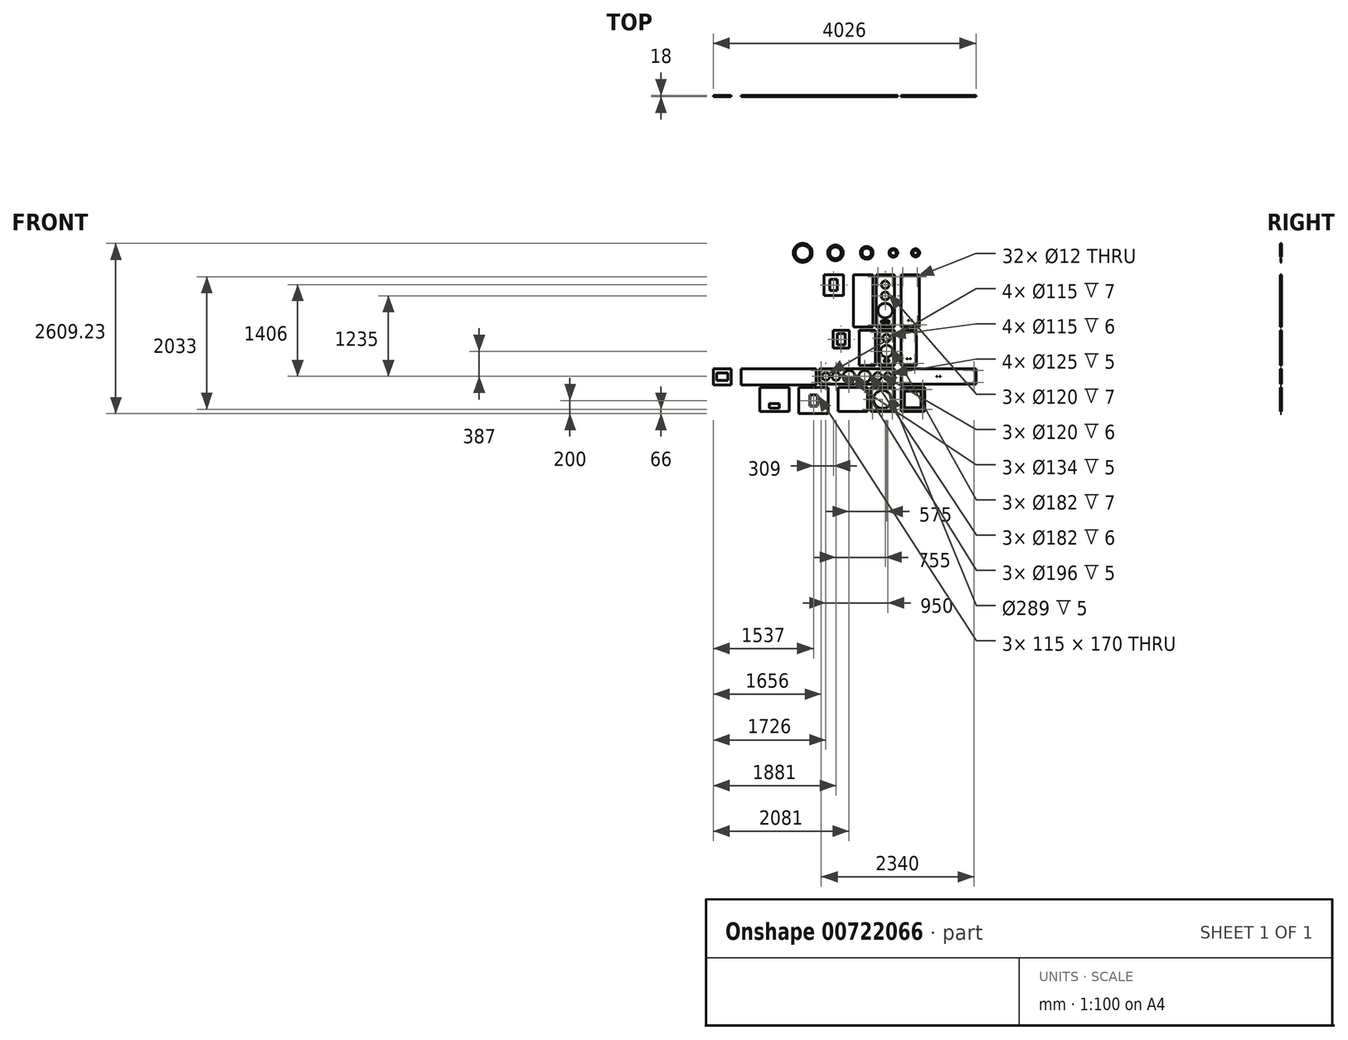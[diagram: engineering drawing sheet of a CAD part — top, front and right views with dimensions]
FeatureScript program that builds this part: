
annotation { "Feature Type Name" : "Feature", "Feature Type Description" : "" }
export const myFeature = defineFeature(function(context is Context, id is Id, definition is map)
    precondition{}
    {
        {
            assignVariable(context, id + "F0", {"name" : "WoodW", "anyValue" : 18});
        }
        {
            var Q0;
            Q0=qCreatedBy(makeId("Front.planeOp"),FACE);
            var sketch = newSketch(context, id + "F1", { "sketchPlane" : qUnion([Q0])});
            skLineSegment(sketch, "E0.bottom", {"start": v(0, 400) * mm, "end": v(-280, 400) * mm});
            skLineSegment(sketch, "E0.top", {"start": v(0, -400) * mm, "end": v(-280, -400) * mm});
            skLineSegment(sketch, "E0.left", {"start": v(0, 400) * mm, "end": v(0, -400) * mm});
            skLineSegment(sketch, "E0.right", {"start": v(-280, 400) * mm, "end": v(-280, -400) * mm});
            skLineSegment(sketch, "E1", {"start": v(-140, 400) * mm, "end": v(-140, -400) * mm, "construction": true});
            skCircle(sketch, "E2", {"center": v(-250, 370) * mm, "radius": 6 * mm});
            skCircle(sketch, "E3.MirrorC", {"center": v(-30, 370) * mm, "radius": 6 * mm});
            skCircle(sketch, "E4.MirrorC", {"center": v(-30, -370) * mm, "radius": 6 * mm});
            skCircle(sketch, "E5.MirrorC", {"center": v(-250, -370) * mm, "radius": 6 * mm});
            skLineSegment(sketch, "E6", {"start": v(50, 227.38) * mm, "end": v(50, -1997.12) * mm, "construction": true});
            skCircle(sketch, "E7.MirrorC", {"center": v(350, -370) * mm, "radius": 6 * mm});
            skCircle(sketch, "E8.MirrorC", {"center": v(130, -370) * mm, "radius": 6 * mm});
            skCircle(sketch, "E9.MirrorC", {"center": v(130, 370) * mm, "radius": 6 * mm});
            skCircle(sketch, "E10.MirrorC", {"center": v(350, 370) * mm, "radius": 6 * mm});
            skLineSegment(sketch, "E11.MirrorCS", {"start": v(100, 400) * mm, "end": v(380, 400) * mm});
            skLineSegment(sketch, "E12.MirrorCS", {"start": v(100, -400) * mm, "end": v(380, -400) * mm});
            skLineSegment(sketch, "E13.MirrorCS", {"start": v(100, 400) * mm, "end": v(100, -400) * mm});
            skLineSegment(sketch, "E14.MirrorCS", {"start": v(380, 400) * mm, "end": v(380, -400) * mm});
            skCircle(sketch, "E15", {"center": v(-140, -150) * mm, "radius": 112.5 * mm});
            skCircle(sketch, "E16", {"center": v(-140, 76) * mm, "radius": 60 * mm});
            skCircle(sketch, "E17", {"center": v(-140, 247) * mm, "radius": 57.5 * mm});
            skCircle(sketch, "E18.1.0", {"center": v(215, -300) * mm, "radius": 3.5 * mm});
            skLineSegment(sketch, "E19.bottom", {"start": v(-196, -305) * mm, "end": v(-84, -305) * mm});
            skLineSegment(sketch, "E19.top", {"start": v(-196, -345) * mm, "end": v(-84, -345) * mm});
            skLineSegment(sketch, "E19.left", {"start": v(-200, -309) * mm, "end": v(-200, -341) * mm});
            skLineSegment(sketch, "E19.right", {"start": v(-80, -309) * mm, "end": v(-80, -341) * mm});
            skPoint(sketch, "E20", {"position": v(-140, -305) * mm});
            skPoint(sketch, "E21.visualSharp", {"position": v(-200, -305) * mm});
            skArc(sketch, "E21.filletArc", {"start": v(-196, -305) * mm, "mid": v(-198.83, -306.17) * mm, "end": v(-200, -309) * mm});
            skPoint(sketch, "E22.visualSharp", {"position": v(-200, -345) * mm});
            skArc(sketch, "E22.filletArc", {"start": v(-200, -341) * mm, "mid": v(-198.83, -343.83) * mm, "end": v(-196, -345) * mm});
            skPoint(sketch, "E23.visualSharp", {"position": v(-80, -345) * mm});
            skArc(sketch, "E23.filletArc", {"start": v(-84, -345) * mm, "mid": v(-81.17, -343.83) * mm, "end": v(-80, -341) * mm});
            skPoint(sketch, "E24.visualSharp", {"position": v(-80, -305) * mm});
            skArc(sketch, "E24.filletArc", {"start": v(-80, -309) * mm, "mid": v(-81.17, -306.17) * mm, "end": v(-84, -305) * mm});
            skLineSegment(sketch, "E25.bottom", {"start": v(0, -450) * mm, "end": v(-240, -450) * mm});
            skLineSegment(sketch, "E25.top", {"start": v(0, -989) * mm, "end": v(-240, -989) * mm});
            skLineSegment(sketch, "E25.left", {"start": v(0, -450) * mm, "end": v(0, -989) * mm});
            skLineSegment(sketch, "E25.right", {"start": v(-240, -450) * mm, "end": v(-240, -989) * mm});
            skLineSegment(sketch, "E26", {"start": v(-120, -450) * mm, "end": v(-120, -989) * mm, "construction": true});
            skCircle(sketch, "E27", {"center": v(-120, -571) * mm, "radius": 57.5 * mm});
            skCircle(sketch, "E28", {"center": v(-120, -772) * mm, "radius": 91 * mm});
            skCircle(sketch, "E29", {"center": v(-210, -480) * mm, "radius": 6 * mm});
            skLineSegment(sketch, "E30", {"start": v(-240, -719.5) * mm, "end": v(0, -719.5) * mm, "construction": true});
            skCircle(sketch, "E31.MirrorC", {"center": v(-210, -959) * mm, "radius": 6 * mm});
            skCircle(sketch, "E32.MirrorC", {"center": v(-30, -959) * mm, "radius": 6 * mm});
            skCircle(sketch, "E33.MirrorC", {"center": v(-30, -480) * mm, "radius": 6 * mm});
            skLineSegment(sketch, "E34.MirrorCS", {"start": v(100, -450) * mm, "end": v(100, -989) * mm});
            skLineSegment(sketch, "E35.MirrorCS", {"start": v(100, -450) * mm, "end": v(340, -450) * mm});
            skLineSegment(sketch, "E36.MirrorCS", {"start": v(340, -450) * mm, "end": v(340, -989) * mm});
            skLineSegment(sketch, "E37.MirrorCS", {"start": v(100, -989) * mm, "end": v(340, -989) * mm});
            skCircle(sketch, "E38.MirrorC", {"center": v(130, -959) * mm, "radius": 6 * mm});
            skCircle(sketch, "E39.MirrorC", {"center": v(310, -959) * mm, "radius": 6 * mm});
            skCircle(sketch, "E40.MirrorC", {"center": v(130, -480) * mm, "radius": 6 * mm});
            skCircle(sketch, "E41.MirrorC", {"center": v(310, -480) * mm, "radius": 6 * mm});
            skLineSegment(sketch, "E42.bottom", {"start": v(-153.5, -904) * mm, "end": v(-86.5, -904) * mm});
            skLineSegment(sketch, "E42.top", {"start": v(-153.5, -934) * mm, "end": v(-86.5, -934) * mm});
            skLineSegment(sketch, "E42.left", {"start": v(-157.5, -908) * mm, "end": v(-157.5, -930) * mm});
            skLineSegment(sketch, "E42.right", {"start": v(-82.5, -908) * mm, "end": v(-82.5, -930) * mm});
            skPoint(sketch, "E43", {"position": v(-120, -904) * mm});
            skLineSegment(sketch, "E44", {"start": v(220, -450) * mm, "end": v(220, -989) * mm, "construction": true});
            skPoint(sketch, "E45.visualSharp", {"position": v(-157.5, -904) * mm});
            skArc(sketch, "E45.filletArc", {"start": v(-153.5, -904) * mm, "mid": v(-156.33, -905.17) * mm, "end": v(-157.5, -908) * mm});
            skPoint(sketch, "E46.visualSharp", {"position": v(-157.5, -934) * mm});
            skArc(sketch, "E46.filletArc", {"start": v(-157.5, -930) * mm, "mid": v(-156.33, -932.83) * mm, "end": v(-153.5, -934) * mm});
            skPoint(sketch, "E47.visualSharp", {"position": v(-82.5, -934) * mm});
            skArc(sketch, "E47.filletArc", {"start": v(-86.5, -934) * mm, "mid": v(-83.67, -932.83) * mm, "end": v(-82.5, -930) * mm});
            skPoint(sketch, "E48.visualSharp", {"position": v(-82.5, -904) * mm});
            skArc(sketch, "E48.filletArc", {"start": v(-82.5, -908) * mm, "mid": v(-83.67, -905.17) * mm, "end": v(-86.5, -904) * mm});
            skLineSegment(sketch, "E49.bottom", {"start": v(0, -1039) * mm, "end": v(-1150, -1039) * mm});
            skLineSegment(sketch, "E49.top", {"start": v(0, -1279) * mm, "end": v(-1150, -1279) * mm});
            skLineSegment(sketch, "E49.left", {"start": v(0, -1039) * mm, "end": v(0, -1279) * mm});
            skLineSegment(sketch, "E49.right", {"start": v(-1150, -1039) * mm, "end": v(-1150, -1279) * mm});
            skLineSegment(sketch, "E50", {"start": v(-1150, -1159) * mm, "end": v(0, -1159) * mm, "construction": true});
            skLineSegment(sketch, "E51", {"start": v(-575, -1039) * mm, "end": v(-575, -1279) * mm, "construction": true});
            skCircle(sketch, "E52", {"center": v(-1120, -1069) * mm, "radius": 6 * mm});
            skCircle(sketch, "E53.MirrorC", {"center": v(-1120, -1249) * mm, "radius": 6 * mm});
            skCircle(sketch, "E54.MirrorC", {"center": v(-30, -1249) * mm, "radius": 6 * mm});
            skCircle(sketch, "E55.MirrorC", {"center": v(-30, -1069) * mm, "radius": 6 * mm});
            skCircle(sketch, "E56.MirrorC", {"center": v(130, -1069) * mm, "radius": 6 * mm});
            skCircle(sketch, "E57.MirrorC", {"center": v(130, -1249) * mm, "radius": 6 * mm});
            skCircle(sketch, "E58.MirrorC", {"center": v(1220, -1069) * mm, "radius": 6 * mm});
            skLineSegment(sketch, "E59.MirrorCS", {"start": v(1250, -1159) * mm, "end": v(100, -1159) * mm, "construction": true});
            skCircle(sketch, "E60.MirrorC", {"center": v(1220, -1249) * mm, "radius": 6 * mm});
            skLineSegment(sketch, "E61.MirrorCS", {"start": v(1250, -1039) * mm, "end": v(1250, -1279) * mm});
            skLineSegment(sketch, "E62.MirrorCS", {"start": v(675, -1039) * mm, "end": v(675, -1279) * mm, "construction": true});
            skLineSegment(sketch, "E63.MirrorCS", {"start": v(100, -1039) * mm, "end": v(100, -1279) * mm});
            skLineSegment(sketch, "E64.MirrorCS", {"start": v(100, -1039) * mm, "end": v(1250, -1039) * mm});
            skLineSegment(sketch, "E65.MirrorCS", {"start": v(100, -1279) * mm, "end": v(1250, -1279) * mm});
            skCircle(sketch, "E66", {"center": v(-100, -1159) * mm, "radius": 57.5 * mm});
            skCircle(sketch, "E67", {"center": v(-255, -1159) * mm, "radius": 60 * mm});
            skCircle(sketch, "E68", {"center": v(-455, -1159) * mm, "radius": 91 * mm});
            skCircle(sketch, "E69.MirrorC", {"center": v(-895, -1159) * mm, "radius": 60 * mm});
            skCircle(sketch, "E70.MirrorC", {"center": v(-1050, -1159) * mm, "radius": 57.5 * mm});
            skCircle(sketch, "E71.MirrorC", {"center": v(-695, -1159) * mm, "radius": 91 * mm});
            skLineSegment(sketch, "E72.bottom", {"start": v(0, -1329) * mm, "end": v(-364, -1329) * mm});
            skLineSegment(sketch, "E72.top", {"start": v(0, -1693) * mm, "end": v(-364, -1693) * mm});
            skLineSegment(sketch, "E72.left", {"start": v(0, -1329) * mm, "end": v(0, -1693) * mm});
            skLineSegment(sketch, "E72.right", {"start": v(-364, -1329) * mm, "end": v(-364, -1693) * mm});
            skLineSegment(sketch, "E73", {"start": v(-182, -1329) * mm, "end": v(-182, -1693) * mm, "construction": true});
            skLineSegment(sketch, "E74", {"start": v(-364, -1511) * mm, "end": v(0, -1511) * mm, "construction": true});
            skCircle(sketch, "E75", {"center": v(-334, -1359) * mm, "radius": 6 * mm});
            skCircle(sketch, "E76.MirrorC", {"center": v(-30, -1359) * mm, "radius": 6 * mm});
            skCircle(sketch, "E77.MirrorC", {"center": v(-334, -1663) * mm, "radius": 6 * mm});
            skCircle(sketch, "E78.MirrorC", {"center": v(-30, -1663) * mm, "radius": 6 * mm});
            skCircle(sketch, "E79.MirrorC", {"center": v(130, -1663) * mm, "radius": 6 * mm});
            skCircle(sketch, "E80.MirrorC", {"center": v(434, -1663) * mm, "radius": 6 * mm});
            skCircle(sketch, "E81.MirrorC", {"center": v(434, -1359) * mm, "radius": 6 * mm});
            skCircle(sketch, "E82.MirrorC", {"center": v(130, -1359) * mm, "radius": 6 * mm});
            skLineSegment(sketch, "E83.MirrorCS", {"start": v(464, -1329) * mm, "end": v(464, -1693) * mm});
            skLineSegment(sketch, "E84.MirrorCS", {"start": v(100, -1329) * mm, "end": v(100, -1693) * mm});
            skLineSegment(sketch, "E85.MirrorCS", {"start": v(100, -1693) * mm, "end": v(464, -1693) * mm});
            skLineSegment(sketch, "E86.MirrorCS", {"start": v(282, -1329) * mm, "end": v(282, -1693) * mm, "construction": true});
            skLineSegment(sketch, "E87.MirrorCS", {"start": v(100, -1329) * mm, "end": v(464, -1329) * mm});
            skLineSegment(sketch, "E88.MirrorCS", {"start": v(464, -1511) * mm, "end": v(100, -1511) * mm, "construction": true});
            skCircle(sketch, "E89", {"center": v(-182, -1511) * mm, "radius": 137.5 * mm});
            skLineSegment(sketch, "E90.bottom", {"start": v(158.5, -1383.5) * mm, "end": v(405.5, -1383.5) * mm});
            skLineSegment(sketch, "E90.top", {"start": v(158.5, -1638.5) * mm, "end": v(405.5, -1638.5) * mm});
            skLineSegment(sketch, "E90.left", {"start": v(154.5, -1387.5) * mm, "end": v(154.5, -1634.5) * mm});
            skLineSegment(sketch, "E90.right", {"start": v(409.5, -1387.5) * mm, "end": v(409.5, -1634.5) * mm});
            skPoint(sketch, "E91", {"position": v(282, -1383.5) * mm});
            skLineSegment(sketch, "E92", {"start": v(154.5, -1511) * mm, "end": v(409.5, -1511) * mm, "construction": true});
            skPoint(sketch, "E93.visualSharp", {"position": v(154.5, -1383.5) * mm});
            skArc(sketch, "E93.filletArc", {"start": v(158.5, -1383.5) * mm, "mid": v(155.67, -1384.67) * mm, "end": v(154.5, -1387.5) * mm});
            skPoint(sketch, "E94.visualSharp", {"position": v(154.5, -1638.5) * mm});
            skArc(sketch, "E94.filletArc", {"start": v(154.5, -1634.5) * mm, "mid": v(155.67, -1637.33) * mm, "end": v(158.5, -1638.5) * mm});
            skPoint(sketch, "E95.visualSharp", {"position": v(409.5, -1638.5) * mm});
            skArc(sketch, "E95.filletArc", {"start": v(405.5, -1638.5) * mm, "mid": v(408.33, -1637.33) * mm, "end": v(409.5, -1634.5) * mm});
            skPoint(sketch, "E96.visualSharp", {"position": v(409.5, -1383.5) * mm});
            skArc(sketch, "E96.filletArc", {"start": v(409.5, -1387.5) * mm, "mid": v(408.33, -1384.67) * mm, "end": v(405.5, -1383.5) * mm});
            skLineSegment(sketch, "E97", {"start": v(240, -400) * mm, "end": v(240, 400) * mm, "construction": true});
            skCircle(sketch, "E98.MirrorC", {"center": v(265, -300) * mm, "radius": 3.5 * mm});
            skCircle(sketch, "E99", {"center": v(195, -889) * mm, "radius": 3.5 * mm});
            skCircle(sketch, "E100.MirrorC", {"center": v(245, -889) * mm, "radius": 3.5 * mm});
            skCircle(sketch, "E101", {"center": v(650, -1159) * mm, "radius": 3.5 * mm});
            skCircle(sketch, "E102.MirrorC", {"center": v(700, -1159) * mm, "radius": 3.5 * mm});
            skSolve(sketch);
        }
        {
            var Q0;
            Q0 = qSketchRegion(id + "F1", true);
            extrude(context, id + "F2", {"entities" : qUnion([Q0]), "depth" : 18 * mm, "offsetDistance" : 25 * mm});
        }
        {
            var Q0;
            Q0=qCreatedBy(makeId("Front.planeOp"),FACE);
            var sketch = newSketch(context, id + "F3", { "sketchPlane" : qUnion([Q0])});
            skLineSegment(sketch, "E103.bottom", {"start": v(-330, 400) * mm, "end": v(-630, 400) * mm});
            skLineSegment(sketch, "E103.top", {"start": v(-330, -400) * mm, "end": v(-630, -400) * mm});
            skLineSegment(sketch, "E103.left", {"start": v(-330, 400) * mm, "end": v(-330, -400) * mm});
            skLineSegment(sketch, "E103.right", {"start": v(-630, 400) * mm, "end": v(-630, -400) * mm});
            skLineSegment(sketch, "E104.bottom", {"start": v(-780, 400) * mm, "end": v(-1080, 400) * mm});
            skLineSegment(sketch, "E104.top", {"start": v(-780, 84) * mm, "end": v(-1080, 84) * mm});
            skLineSegment(sketch, "E104.left", {"start": v(-780, 400) * mm, "end": v(-780, 84) * mm});
            skLineSegment(sketch, "E104.right", {"start": v(-1080, 400) * mm, "end": v(-1080, 84) * mm});
            skLineSegment(sketch, "E105.bottom", {"start": v(-290, -450) * mm, "end": v(-540, -450) * mm});
            skLineSegment(sketch, "E105.top", {"start": v(-290, -989) * mm, "end": v(-540, -989) * mm});
            skLineSegment(sketch, "E105.left", {"start": v(-290, -450) * mm, "end": v(-290, -989) * mm});
            skLineSegment(sketch, "E105.right", {"start": v(-540, -450) * mm, "end": v(-540, -989) * mm});
            skLineSegment(sketch, "E106.bottom", {"start": v(-690, -450) * mm, "end": v(-940, -450) * mm});
            skLineSegment(sketch, "E106.top", {"start": v(-690, -726) * mm, "end": v(-940, -726) * mm});
            skLineSegment(sketch, "E106.left", {"start": v(-690, -450) * mm, "end": v(-690, -726) * mm});
            skLineSegment(sketch, "E106.right", {"start": v(-940, -450) * mm, "end": v(-940, -726) * mm});
            skLineSegment(sketch, "E107.bottom", {"start": v(-1200, -1039) * mm, "end": v(-2350, -1039) * mm});
            skLineSegment(sketch, "E107.top", {"start": v(-1200, -1289) * mm, "end": v(-2350, -1289) * mm});
            skLineSegment(sketch, "E107.left", {"start": v(-1200, -1039) * mm, "end": v(-1200, -1289) * mm});
            skLineSegment(sketch, "E107.right", {"start": v(-2350, -1039) * mm, "end": v(-2350, -1289) * mm});
            skLineSegment(sketch, "E108.bottom", {"start": v(-2500, -1039) * mm, "end": v(-2776, -1039) * mm});
            skLineSegment(sketch, "E108.top", {"start": v(-2500, -1289) * mm, "end": v(-2776, -1289) * mm});
            skLineSegment(sketch, "E108.left", {"start": v(-2500, -1039) * mm, "end": v(-2500, -1289) * mm});
            skLineSegment(sketch, "E108.right", {"start": v(-2776, -1039) * mm, "end": v(-2776, -1289) * mm});
            skLineSegment(sketch, "E109.bottom", {"start": v(-414, -1329) * mm, "end": v(-864, -1329) * mm});
            skLineSegment(sketch, "E109.top", {"start": v(-414, -1693) * mm, "end": v(-864, -1693) * mm});
            skLineSegment(sketch, "E109.left", {"start": v(-414, -1329) * mm, "end": v(-414, -1693) * mm});
            skLineSegment(sketch, "E109.right", {"start": v(-864, -1329) * mm, "end": v(-864, -1693) * mm});
            skLineSegment(sketch, "E110.bottom", {"start": v(-1014, -1329) * mm, "end": v(-1464, -1329) * mm});
            skLineSegment(sketch, "E110.top", {"start": v(-1014, -1729) * mm, "end": v(-1464, -1729) * mm});
            skLineSegment(sketch, "E110.left", {"start": v(-1014, -1329) * mm, "end": v(-1014, -1729) * mm});
            skLineSegment(sketch, "E110.right", {"start": v(-1464, -1329) * mm, "end": v(-1464, -1729) * mm});
            skLineSegment(sketch, "E111.bottom", {"start": v(-987.5, 327) * mm, "end": v(-872.5, 327) * mm});
            skLineSegment(sketch, "E111.top", {"start": v(-987.5, 157) * mm, "end": v(-872.5, 157) * mm});
            skLineSegment(sketch, "E111.left", {"start": v(-987.5, 327) * mm, "end": v(-987.5, 157) * mm});
            skLineSegment(sketch, "E111.right", {"start": v(-872.5, 327) * mm, "end": v(-872.5, 157) * mm});
            skLineSegment(sketch, "E112", {"start": v(-930, 400) * mm, "end": v(-930, 84) * mm, "construction": true});
            skLineSegment(sketch, "E113", {"start": v(-1080, 242) * mm, "end": v(-780, 242) * mm, "construction": true});
            skPoint(sketch, "E114", {"position": v(-930, 327) * mm});
            skPoint(sketch, "E115", {"position": v(-987.5, 242) * mm});
            skLineSegment(sketch, "E116", {"start": v(-815, -450) * mm, "end": v(-815, -726) * mm, "construction": true});
            skLineSegment(sketch, "E117", {"start": v(-940, -588) * mm, "end": v(-690, -588) * mm, "construction": true});
            skLineSegment(sketch, "E118.bottom", {"start": v(-872.5, -503) * mm, "end": v(-757.5, -503) * mm});
            skLineSegment(sketch, "E118.top", {"start": v(-872.5, -673) * mm, "end": v(-757.5, -673) * mm});
            skLineSegment(sketch, "E118.left", {"start": v(-872.5, -503) * mm, "end": v(-872.5, -673) * mm});
            skLineSegment(sketch, "E118.right", {"start": v(-757.5, -503) * mm, "end": v(-757.5, -673) * mm});
            skPoint(sketch, "E119", {"position": v(-815, -503) * mm});
            skPoint(sketch, "E120", {"position": v(-757.5, -588) * mm});
            skLineSegment(sketch, "E121", {"start": v(-2638, -1039) * mm, "end": v(-2638, -1289) * mm, "construction": true});
            skLineSegment(sketch, "E122", {"start": v(-2500, -1164) * mm, "end": v(-2776, -1164) * mm, "construction": true});
            skLineSegment(sketch, "E123.bottom", {"start": v(-2553, -1221.5) * mm, "end": v(-2723, -1221.5) * mm});
            skLineSegment(sketch, "E123.top", {"start": v(-2553, -1106.5) * mm, "end": v(-2723, -1106.5) * mm});
            skLineSegment(sketch, "E123.left", {"start": v(-2553, -1221.5) * mm, "end": v(-2553, -1106.5) * mm});
            skLineSegment(sketch, "E123.right", {"start": v(-2723, -1221.5) * mm, "end": v(-2723, -1106.5) * mm});
            skPoint(sketch, "E124", {"position": v(-2638, -1106.5) * mm});
            skPoint(sketch, "E125", {"position": v(-2553, -1164) * mm});
            skLineSegment(sketch, "E126", {"start": v(-1239, -1329) * mm, "end": v(-1239, -1729) * mm, "construction": true});
            skLineSegment(sketch, "E127", {"start": v(-1014, -1529) * mm, "end": v(-1464, -1529) * mm, "construction": true});
            skLineSegment(sketch, "E128.bottom", {"start": v(-1181.5, -1614) * mm, "end": v(-1296.5, -1614) * mm});
            skLineSegment(sketch, "E128.top", {"start": v(-1181.5, -1444) * mm, "end": v(-1296.5, -1444) * mm});
            skLineSegment(sketch, "E128.left", {"start": v(-1181.5, -1614) * mm, "end": v(-1181.5, -1444) * mm});
            skLineSegment(sketch, "E128.right", {"start": v(-1296.5, -1614) * mm, "end": v(-1296.5, -1444) * mm});
            skPoint(sketch, "E129", {"position": v(-1239, -1444) * mm});
            skPoint(sketch, "E130", {"position": v(-1181.5, -1529) * mm});
            skLineSegment(sketch, "E131.bottom", {"start": v(-1614, -1329) * mm, "end": v(-2064, -1329) * mm});
            skLineSegment(sketch, "E131.top", {"start": v(-1614, -1693) * mm, "end": v(-2064, -1693) * mm});
            skLineSegment(sketch, "E131.left", {"start": v(-1614, -1329) * mm, "end": v(-1614, -1693) * mm});
            skLineSegment(sketch, "E131.right", {"start": v(-2064, -1329) * mm, "end": v(-2064, -1693) * mm});
            skLineSegment(sketch, "E132.bottom", {"start": v(-1910, -1573) * mm, "end": v(-1768, -1573) * mm});
            skLineSegment(sketch, "E132.top", {"start": v(-1910, -1643) * mm, "end": v(-1768, -1643) * mm});
            skLineSegment(sketch, "E132.left", {"start": v(-1914, -1577) * mm, "end": v(-1914, -1639) * mm});
            skLineSegment(sketch, "E132.right", {"start": v(-1764, -1577) * mm, "end": v(-1764, -1639) * mm});
            skLineSegment(sketch, "E133", {"start": v(-1839, -1329) * mm, "end": v(-1839, -1693) * mm, "construction": true});
            skPoint(sketch, "E134", {"position": v(-1839, -1573) * mm});
            skPoint(sketch, "E135.visualSharp", {"position": v(-1764, -1573) * mm});
            skArc(sketch, "E135.filletArc", {"start": v(-1764, -1577) * mm, "mid": v(-1765.17, -1574.17) * mm, "end": v(-1768, -1573) * mm});
            skPoint(sketch, "E136.visualSharp", {"position": v(-1764, -1643) * mm});
            skArc(sketch, "E136.filletArc", {"start": v(-1768, -1643) * mm, "mid": v(-1765.17, -1641.83) * mm, "end": v(-1764, -1639) * mm});
            skPoint(sketch, "E137.visualSharp", {"position": v(-1914, -1643) * mm});
            skArc(sketch, "E137.filletArc", {"start": v(-1914, -1639) * mm, "mid": v(-1912.83, -1641.83) * mm, "end": v(-1910, -1643) * mm});
            skPoint(sketch, "E138.visualSharp", {"position": v(-1914, -1573) * mm});
            skArc(sketch, "E138.filletArc", {"start": v(-1910, -1573) * mm, "mid": v(-1912.83, -1574.17) * mm, "end": v(-1914, -1577) * mm});
            skSolve(sketch);
        }
        {
            var Q0;
            Q0 = qSketchRegion(id + "F3", true);
            extrude(context, id + "F4", {"entities" : qUnion([Q0]), "depth" : (getVariable(context, 'WoodW')) * mm, "offsetDistance" : 25 * mm});
        }
        {
            var Q0;
            Q0=qCreatedBy(makeId("Front.planeOp"),FACE);
            var sketch = newSketch(context, id + "F5", { "sketchPlane" : qUnion([Q0])});
            skCircle(sketch, "E139", {"center": v(-1404.17, 735.73) * mm, "radius": 137.5 * mm});
            skCircle(sketch, "E140", {"center": v(-903.37, 735.73) * mm, "radius": 112.5 * mm});
            skCircle(sketch, "E141", {"center": v(-423.44, 735.73) * mm, "radius": 91 * mm});
            skCircle(sketch, "E142", {"center": v(-16.54, 735.73) * mm, "radius": 46 * mm});
            skCircle(sketch, "E143", {"center": v(324.28, 735.73) * mm, "radius": 57.5 * mm});
            skCircle(sketch, "E144", {"center": v(-1404.17, 735.73) * mm, "radius": 116 * mm});
            skCircle(sketch, "E145", {"center": v(-903.37, 735.73) * mm, "radius": 89 * mm});
            skCircle(sketch, "E146", {"center": v(-423.44, 735.73) * mm, "radius": 71 * mm});
            skCircle(sketch, "E147", {"center": v(-16.54, 735.73) * mm, "radius": 60 * mm});
            skCircle(sketch, "E148", {"center": v(324.28, 735.73) * mm, "radius": 37 * mm});
            skSolve(sketch);
        }
        {
            var Q0;
            Q0 = qSketchRegion(id + "F5", true);
            extrude(context, id + "F6", {"entities" : qUnion([Q0]), "depth" : 18 * mm, "offsetDistance" : 25 * mm});
        }
        {
            var Q0;
            Q0=qCreatedBy(makeId("Front.planeOp"),FACE);
            cPlane(context, id + "F7", {"entities" : qUnion([Q0]), "cplaneType" : CPlaneType.OFFSET, "offset" : 7 * mm, "width" : 150 * mm, "height" : 150 * mm});
        }
        {
            var Q0;
            Q0=qCreatedBy(id+"F7.planeOp",FACE);
            var sketch = newSketch(context, id + "F8", { "sketchPlane" : qUnion([Q0])});
            skCircle(sketch, "E149", {"center": v(324.28, 735.73) * mm, "radius": 62.5 * mm});
            skCircle(sketch, "E150", {"center": v(324.28, 735.73) * mm, "radius": 37 * mm});
            skCircle(sketch, "E151", {"center": v(-16.54, 735.73) * mm, "radius": 46 * mm});
            skCircle(sketch, "E152", {"center": v(-16.54, 735.73) * mm, "radius": 67 * mm});
            skCircle(sketch, "E153", {"center": v(-423.44, 735.73) * mm, "radius": 71 * mm});
            skCircle(sketch, "E154", {"center": v(-423.44, 735.73) * mm, "radius": 98 * mm});
            skCircle(sketch, "E155", {"center": v(-903.37, 735.73) * mm, "radius": 89 * mm});
            skCircle(sketch, "E156", {"center": v(-903.37, 735.73) * mm, "radius": 119.5 * mm});
            skCircle(sketch, "E157", {"center": v(-1404.17, 735.73) * mm, "radius": 116 * mm});
            skCircle(sketch, "E158", {"center": v(-1404.17, 735.73) * mm, "radius": 144.5 * mm});
            skSolve(sketch);
        }
        {
            var Q0;
            Q0 = qSketchRegion(id + "F8", true);
            extrude(context, id + "F9", {"entities" : qUnion([Q0]), "operationType" : NewBodyOperationType.ADD, "depth" : 4 * mm, "offsetDistance" : 25 * mm});
        }
        {
            var Q0;
            Q0=makeQuery(id+"F6.opExtrude","CAP_EDGE",EDGE,{"disambiguationData":[OSD([sQuery(id+"F5.wireOp",EDGE,"E144")])],"isStart":false});
            var Q1;
            Q1=makeQuery(id+"F6.opExtrude","CAP_EDGE",EDGE,{"disambiguationData":[OSD([sQuery(id+"F5.wireOp",EDGE,"E145")])],"isStart":false});
            var Q2;
            Q2=makeQuery(id+"F6.opExtrude","CAP_EDGE",EDGE,{"disambiguationData":[OSD([sQuery(id+"F5.wireOp",EDGE,"E146")])],"isStart":false});
            var Q3;
            Q3=makeQuery(id+"F6.opExtrude","CAP_EDGE",EDGE,{"disambiguationData":[OSD([sQuery(id+"F5.wireOp",EDGE,"E142")])],"isStart":false});
            var Q4;
            Q4=makeQuery(id+"F6.opExtrude","CAP_EDGE",EDGE,{"disambiguationData":[OSD([sQuery(id+"F5.wireOp",EDGE,"E148")])],"isStart":false});
            chamfer(context, id + "F10", {"entities" : qUnion([Q0, Q1, Q2, Q3, Q4]), "width" : 8 * mm, "tangentPropagation" : true});
        }
        {
            var Q0;
            Q0=qCreatedBy(id+"F7.planeOp",FACE);
            var sketch = newSketch(context, id + "F11", { "sketchPlane" : qUnion([Q0])});
            skCircle(sketch, "E159", {"center": v(-140, 247) * mm, "radius": 62.5 * mm});
            skCircle(sketch, "E160", {"center": v(-140, 76) * mm, "radius": 67 * mm});
            skCircle(sketch, "E161", {"center": v(-140, -150) * mm, "radius": 119.5 * mm});
            skCircle(sketch, "E162", {"center": v(-120, -571) * mm, "radius": 62.5 * mm});
            skCircle(sketch, "E163", {"center": v(-120, -772) * mm, "radius": 98 * mm});
            skCircle(sketch, "E164", {"center": v(-1050, -1159) * mm, "radius": 62.5 * mm});
            skCircle(sketch, "E165", {"center": v(-895, -1159) * mm, "radius": 67 * mm});
            skCircle(sketch, "E166", {"center": v(-695, -1159) * mm, "radius": 98 * mm});
            skCircle(sketch, "E167", {"center": v(-182, -1511) * mm, "radius": 144.5 * mm});
            skLineSegment(sketch, "E168", {"start": v(-575, -1039) * mm, "end": v(-575, -1279) * mm, "construction": true});
            skCircle(sketch, "E169.MirrorC", {"center": v(-455, -1159) * mm, "radius": 98 * mm});
            skCircle(sketch, "E170.MirrorC", {"center": v(-255, -1159) * mm, "radius": 67 * mm});
            skCircle(sketch, "E171.MirrorC", {"center": v(-100, -1159) * mm, "radius": 62.5 * mm});
            skSolve(sketch);
        }
        {
            var Q0;
            Q0 = qSketchRegion(id + "F11", true);
            extrude(context, id + "F12", {"entities" : qUnion([Q0]), "operationType" : NewBodyOperationType.REMOVE, "depth" : 5 * mm, "offsetDistance" : 25 * mm});
        }
    });
